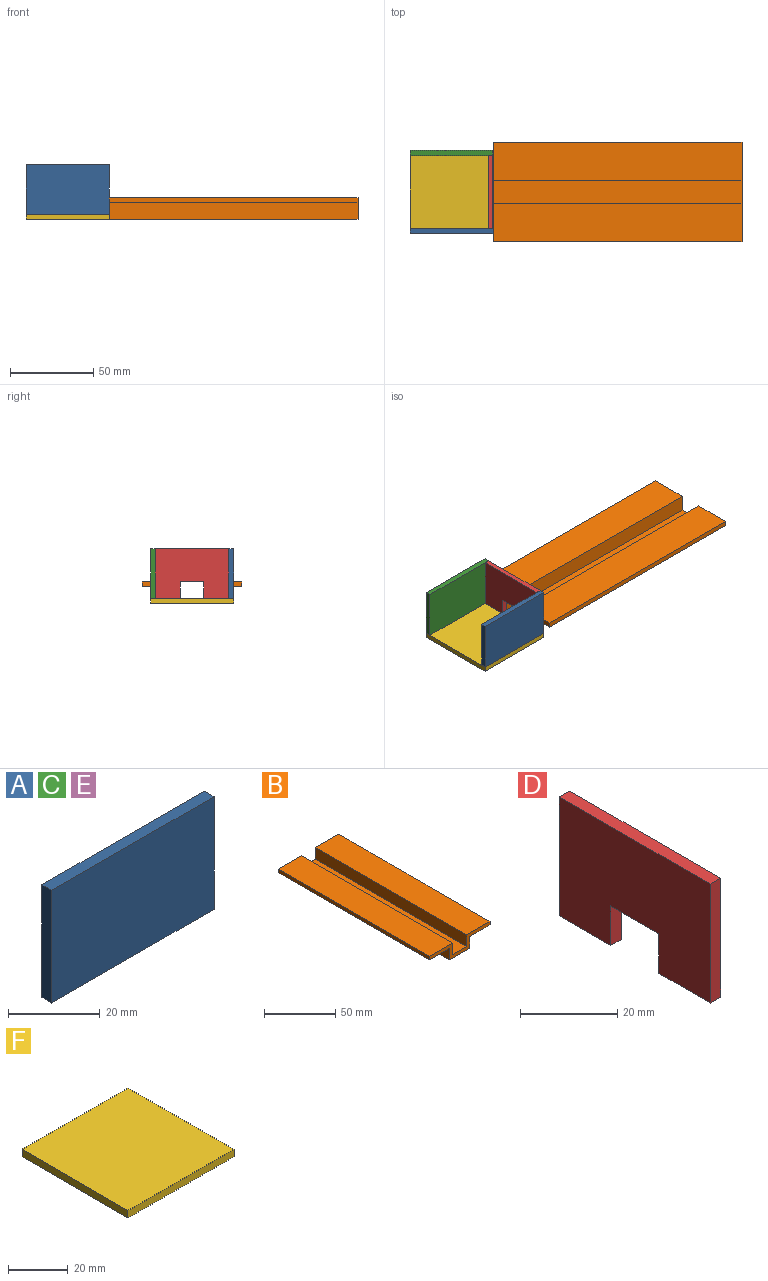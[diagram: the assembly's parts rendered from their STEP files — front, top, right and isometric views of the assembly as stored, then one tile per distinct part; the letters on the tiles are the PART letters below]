
ASSEMBLY  parts=6 mates=4
PART A: 6 faces, bbox 50x3x30 mm
  f0: plane 50x3mm, normal (0,0,1), area 150mm2, adj f1,f3,f4,f5
  f1: plane 30x3mm, normal (-1,0,0), area 90mm2, adj f0,f2,f4,f5
  f2: plane 50x3mm, normal (0,0,-1), area 150mm2, adj f1,f3,f4,f5
  f3: plane 30x3mm, normal (1,0,0), area 90mm2, adj f0,f2,f4,f5
  f4: plane 50x30mm, normal (0,-1,0), area 1500mm2, adj f0,f1,f2,f3
  f5: plane 50x30mm, normal (0,1,0), area 1500mm2, adj f0,f1,f2,f3
PART B: 14 faces, bbox 60x150x13 mm
  f0: plane 150x23mm, normal (0,0,1), area 3450mm2, adj f1,f11,f12,f13
  f1: plane 150x3mm, normal (-1,0,0), area 450mm2, adj f0,f2,f12,f13
  f2: plane 150x20mm, normal (0,0,-1), area 3000mm2, adj f1,f3,f12,f13
  f3: plane 150x10mm, normal (-1,0,0), area 1500mm2, adj f2,f4,f12,f13
  f4: plane 150x20mm, normal (0,0,-1), area 3000mm2, adj f3,f5,f12,f13
  f5: plane 150x10mm, normal (1,0,0), area 1500mm2, adj f4,f6,f12,f13
  f6: plane 150x20mm, normal (0,0,-1), area 3000mm2, adj f5,f7,f12,f13
  f7: plane 150x3mm, normal (1,0,0), area 450mm2, adj f6,f8,f12,f13
  f8: plane 150x23mm, normal (0,0,1), area 3450mm2, adj f7,f9,f12,f13
  f9: plane 150x10mm, normal (-1,0,0), area 1500mm2, adj f8,f10,f12,f13
  f10: plane 150x14mm, normal (0,0,1), area 2100mm2, adj f9,f11,f12,f13
  f11: plane 150x10mm, normal (1,0,0), area 1500mm2, adj f0,f10,f12,f13
  f12: plane 60x13mm, normal (0,-1,0), area 240mm2, adj f0,f1,f2,f3,f4,f5,f6,f7
  f13: plane 60x13mm, normal (0,1,0), area 240mm2, adj f0,f1,f2,f3,f4,f5,f6,f7
PART C: same geometry as A
PART D: 10 faces, bbox 3x44x30 mm
  f0: plane 44x3mm, normal (0,0,1), area 132mm2, adj f1,f7,f8,f9
  f1: plane 30x3mm, normal (0,-1,0), area 90mm2, adj f0,f2,f8,f9
  f2: plane 15x3mm, normal (0,0,-1), area 45mm2, adj f1,f3,f8,f9
  f3: plane 10x3mm, normal (0,1,0), area 30mm2, adj f2,f4,f8,f9
  f4: plane 14x3mm, normal (0,0,-1), area 42mm2, adj f3,f5,f8,f9
  f5: plane 10x3mm, normal (0,-1,0), area 30mm2, adj f4,f6,f8,f9
  f6: plane 15x3mm, normal (0,0,-1), area 45mm2, adj f5,f7,f8,f9
  f7: plane 30x3mm, normal (0,1,0), area 90mm2, adj f0,f6,f8,f9
  f8: plane 44x30mm, normal (1,0,0), area 1180mm2, adj f0,f1,f2,f3,f4,f5,f6,f7
  f9: plane 44x30mm, normal (-1,0,0), area 1180mm2, adj f0,f1,f2,f3,f4,f5,f6,f7
PART E: same geometry as A
PART F: 6 faces, bbox 50x50x3 mm
  f0: plane 50x3mm, normal (0,1,0), area 150mm2, adj f1,f3,f4,f5
  f1: plane 50x3mm, normal (-1,0,0), area 150mm2, adj f0,f2,f4,f5
  f2: plane 50x3mm, normal (0,-1,0), area 150mm2, adj f1,f3,f4,f5
  f3: plane 50x3mm, normal (1,0,0), area 150mm2, adj f0,f2,f4,f5
  f4: plane 50x50mm, normal (0,0,1), area 2500mm2, adj f0,f1,f2,f3
  f5: plane 50x50mm, normal (0,0,-1), area 2500mm2, adj f0,f1,f2,f3
PLACE A t=(-2.44,-49.19,3.23)mm
PLACE B rot(axis=(0,0,-1),90deg) t=(147.56,-53.3,-29.61)mm
PLACE C t=(-2.44,-2.19,3.23)mm
PLACE D t=(-5.44,-79.98,16.07)mm
PLACE E t=(-2.44,-2.19,3.23)mm
PLACE F t=(-8.19,3.09,0.23)mm
MATE parallel F.f4 <-> C.f2  axis (0,0,1) through (-2.44,-2.19,3.23)mm
MATE parallel B.f10 <-> F.f4  axis (0,0,1) through (-2.44,-27.19,3.23)mm
MATE parallel A.f2 <-> F.f4  axis (0,0,1) through (-52.44,-52.19,3.23)mm
MATE parallel D.f6 <-> C.f2  axis (0,0,1) through (-2.44,-5.19,3.23)mm
